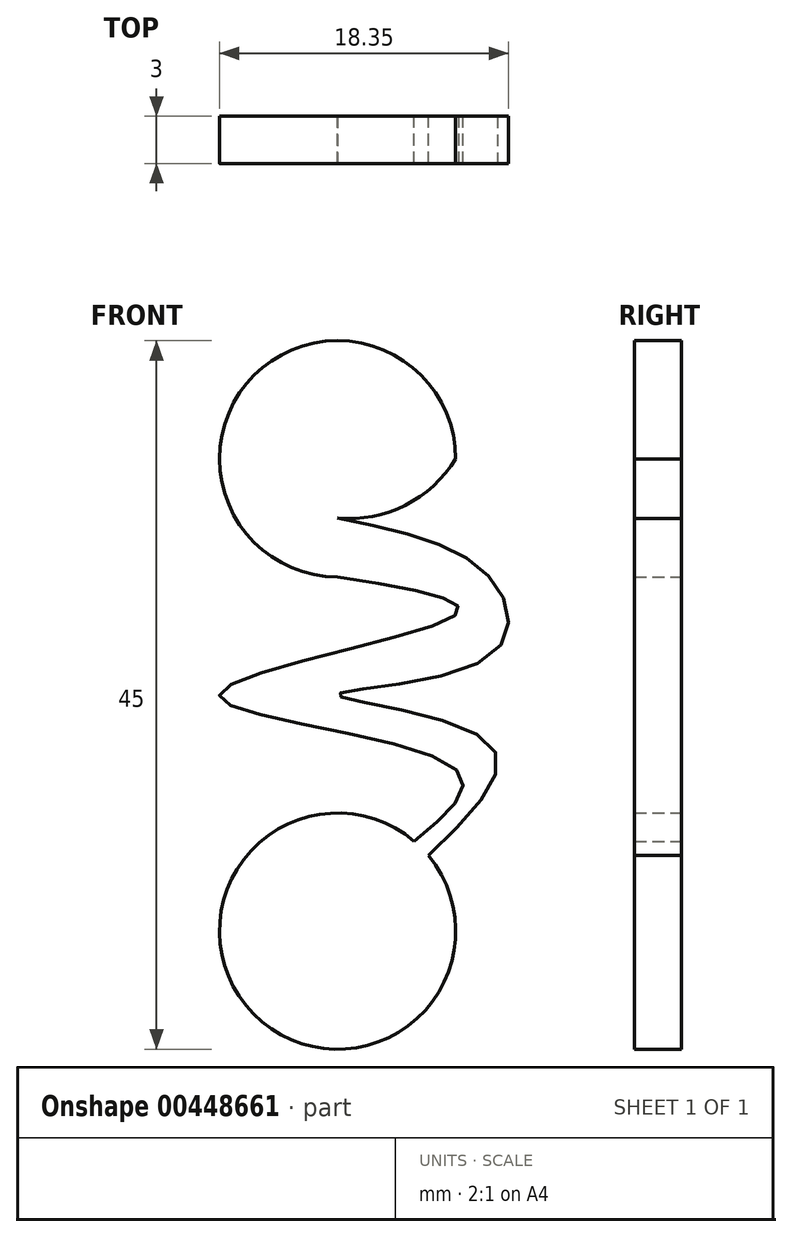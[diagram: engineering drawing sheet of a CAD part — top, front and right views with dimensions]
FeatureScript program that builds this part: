
annotation { "Feature Type Name" : "Feature", "Feature Type Description" : "" }
export const myFeature = defineFeature(function(context is Context, id is Id, definition is map)
    precondition{}
    {
        {
            var Q0;
            Q0=qCreatedBy(makeId("Front.planeOp"),FACE);
            var sketch = newSketch(context, id + "F0", { "sketchPlane" : qUnion([Q0])});
            skArc(sketch, "E0", {"start": v(4.86, 5.7) * mm, "mid": v(-5.33, -5.27) * mm, "end": v(5.76, 4.8) * mm});
            skArc(sketch, "E1", {"start": v(7.5, 30) * mm, "mid": v(-5.3, 35.3) * mm, "end": v(0, 22.5) * mm});
            skLineSegment(sketch, "E2", {"start": v(-7.5, 18.35) * mm, "end": v(-7.5, 18.35) * mm});
            skFitSpline(sketch, "E3", {"points": [v(0, 0) * mm, v(7.5, 14.44) * mm, v(-7.5, 15) * mm, v(7.5, 39.94) * mm, v(0, 22.5) * mm, v(-7.5, 30) * mm], "startDerivative": vector(73.86, 72.54) * mm, "endDerivative": vector(-35.45, 45.29) * mm});
            skArc(sketch, "E4", {"start": v(0, 26.25) * mm, "mid": v(4.3, 27.04) * mm, "end": v(7.5, 30) * mm});
            skPoint(sketch, "E5.orphan", {"position": v(-7.5, 0) * mm});
            skLineSegment(sketch, "E6.trimOffspring", {"start": v(1.87, 1.97) * mm, "end": v(1.87, 1.97) * mm});
            skPoint(sketch, "E7.orphan", {"position": v(7.5, 0) * mm});
            skLineSegment(sketch, "E8", {"start": v(0, 30) * mm, "end": v(0, 0) * mm, "construction": true});
            skFitSpline(sketch, "E9", {"points": [v(0, 22.5) * mm, v(7.5, 20.08) * mm, v(-7.5, 15) * mm, v(7.5, 10.3) * mm, v(4.86, 5.7) * mm], "startDerivative": vector(61.06, -9.73) * mm, "endDerivative": vector(-34.55, -28.3) * mm});
            skFitSpline(sketch, "E10", {"points": [v(0, 26.25) * mm, v(9.63, 22.5) * mm, v(9.63, 17.44) * mm, v(0, 15) * mm, v(9.63, 11.93) * mm, v(5.76, 4.8) * mm], "startDerivative": vector(52.31, -10.74) * mm, "endDerivative": vector(-43.14, -41.67) * mm});
            skSolve(sketch);
        }
        {
            var Q0;
            Q0=qSketchRegion(id+"F0",true);
            extrude(context, id + "F1", {"entities" : qUnion([Q0]), "depth" : 3 * mm});
        }
    });
